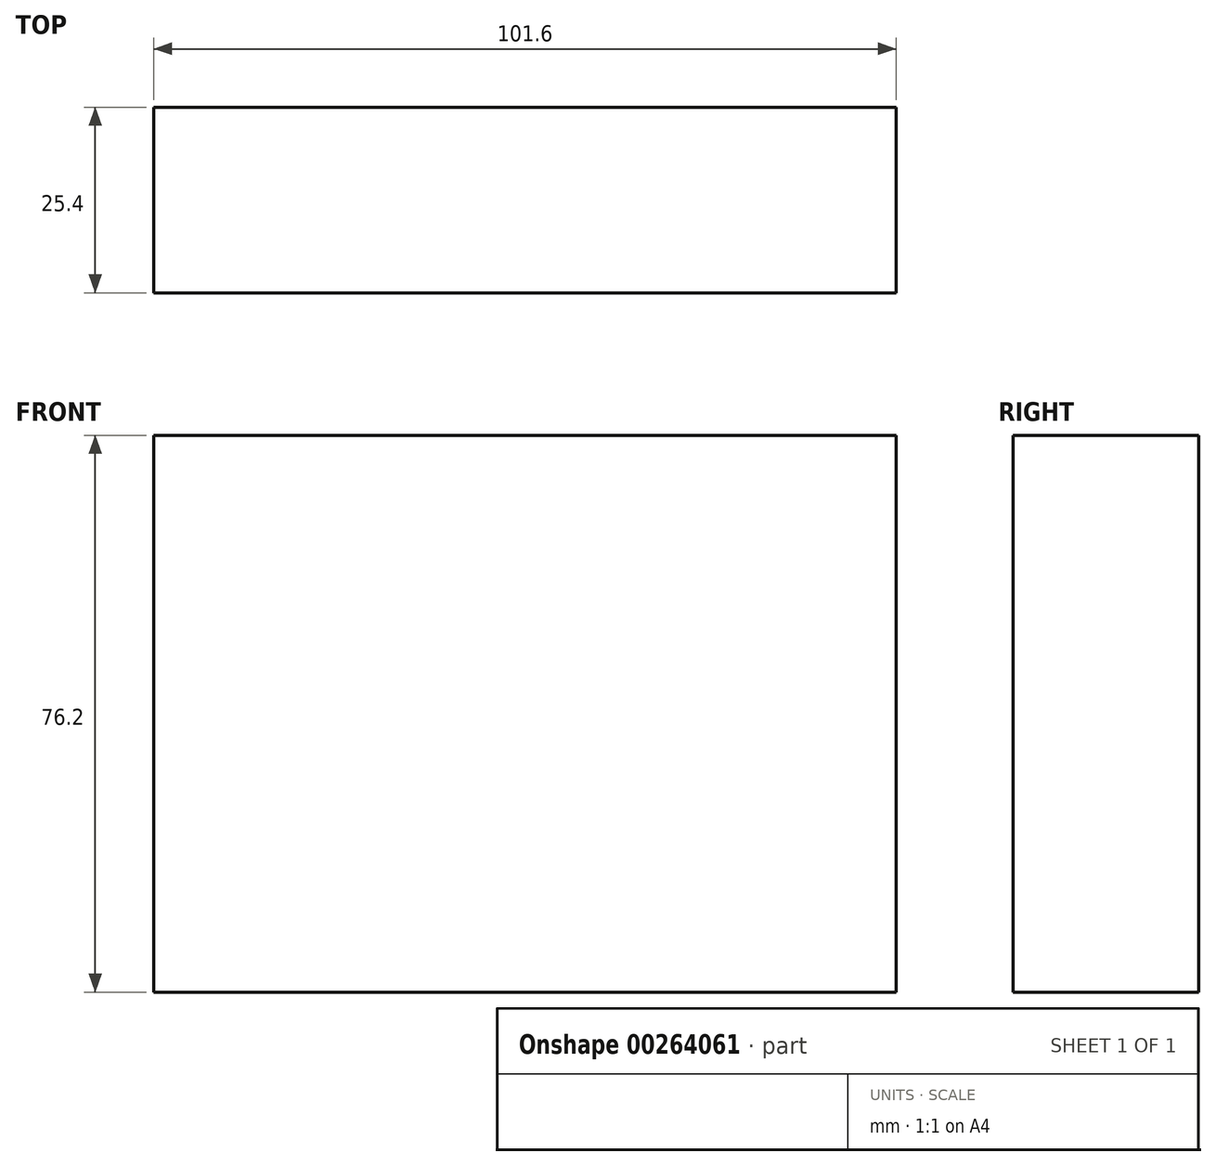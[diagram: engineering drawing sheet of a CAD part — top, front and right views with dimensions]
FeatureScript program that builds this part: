
annotation { "Feature Type Name" : "Feature", "Feature Type Description" : "" }
export const myFeature = defineFeature(function(context is Context, id is Id, definition is map)
    precondition{}
    {
        {
            var Q0;
            Q0=qCreatedBy(makeId("Front.planeOp"),FACE);
            var sketch = newSketch(context, id + "F0", { "sketchPlane" : qUnion([Q0])});
            skLineSegment(sketch, "E0.bottom", {"start": v(0, 0) * mm, "end": v(101.6, 0) * mm});
            skLineSegment(sketch, "E0.top", {"start": v(0, 76.2) * mm, "end": v(101.6, 76.2) * mm});
            skLineSegment(sketch, "E0.left", {"start": v(0, 0) * mm, "end": v(0, 76.2) * mm});
            skLineSegment(sketch, "E0.right", {"start": v(101.6, 0) * mm, "end": v(101.6, 76.2) * mm});
            skSolve(sketch);
        }
        {
            var Q0;
            Q0=makeQuery(id+"F0.imprint","IMPRINT",FACE,{"disambiguationData":[TD([[makeQuery(id+"F0.imprint","IMPRINT",EDGE,{"derivedFrom":sQuery(id+"F0.wireOp",EDGE,"E0.bottom")}),1.0]])]});
            extrude(context, id + "F1", {"entities" : qUnion([Q0]), "oppositeDirection" : true, "depth" : 25.4 * mm});
        }
    });
